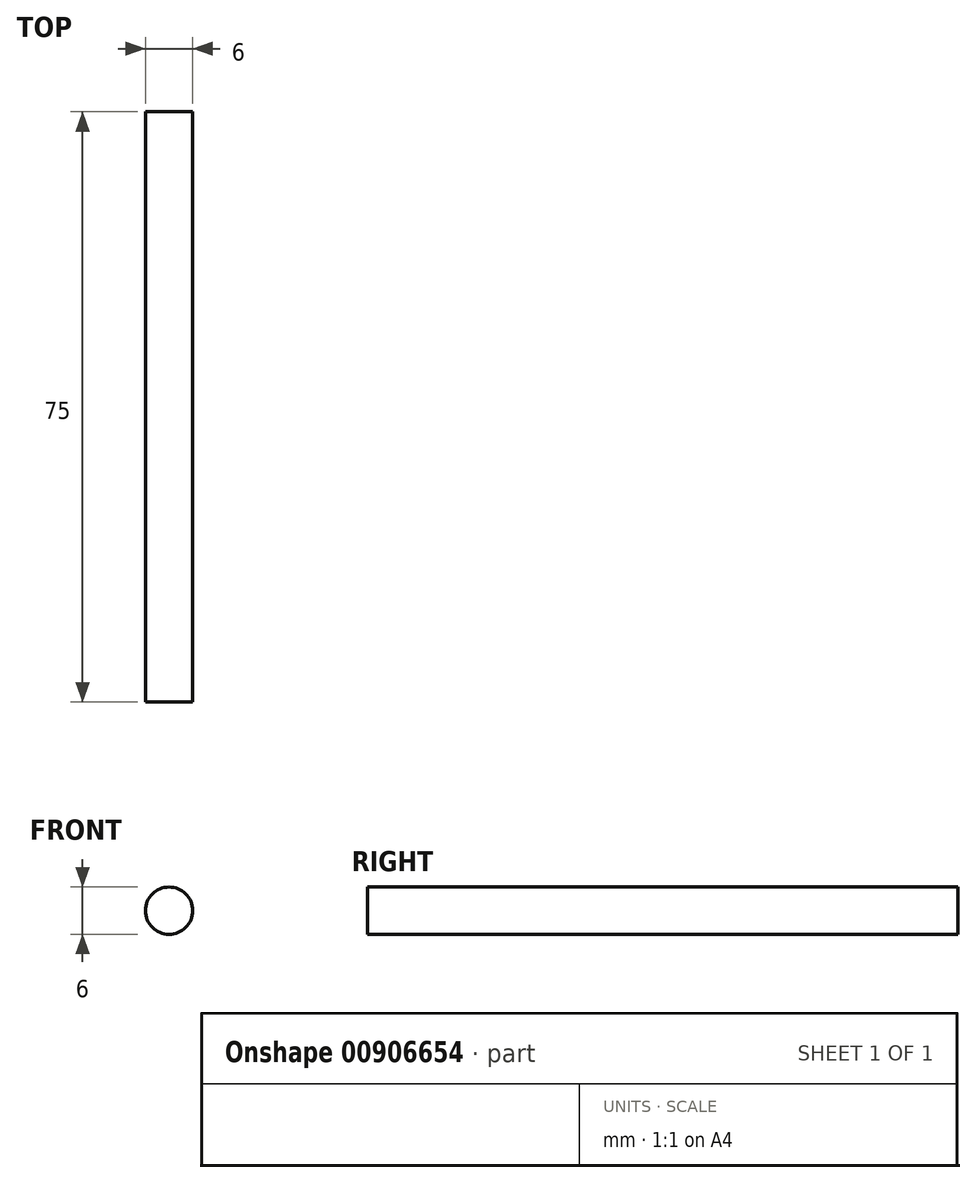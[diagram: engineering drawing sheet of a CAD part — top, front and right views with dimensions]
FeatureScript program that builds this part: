
annotation { "Feature Type Name" : "Feature", "Feature Type Description" : "" }
export const myFeature = defineFeature(function(context is Context, id is Id, definition is map)
    precondition{}
    {
        {
            var Q0;
            Q0=qCreatedBy(makeId("Front.planeOp"),FACE);
            var sketch = newSketch(context, id + "F0", { "sketchPlane" : qUnion([Q0])});
            skCircle(sketch, "E0", {"center": v(0, 0) * mm, "radius": 3 * mm});
            skSolve(sketch);
        }
        {
            var Q0;
            Q0=qSketchRegion(id+"F0",true);
            extrude(context, id + "F1", {"entities" : qUnion([Q0]), "depth" : 75 * mm, "offsetDistance" : 25 * mm});
        }
    });
